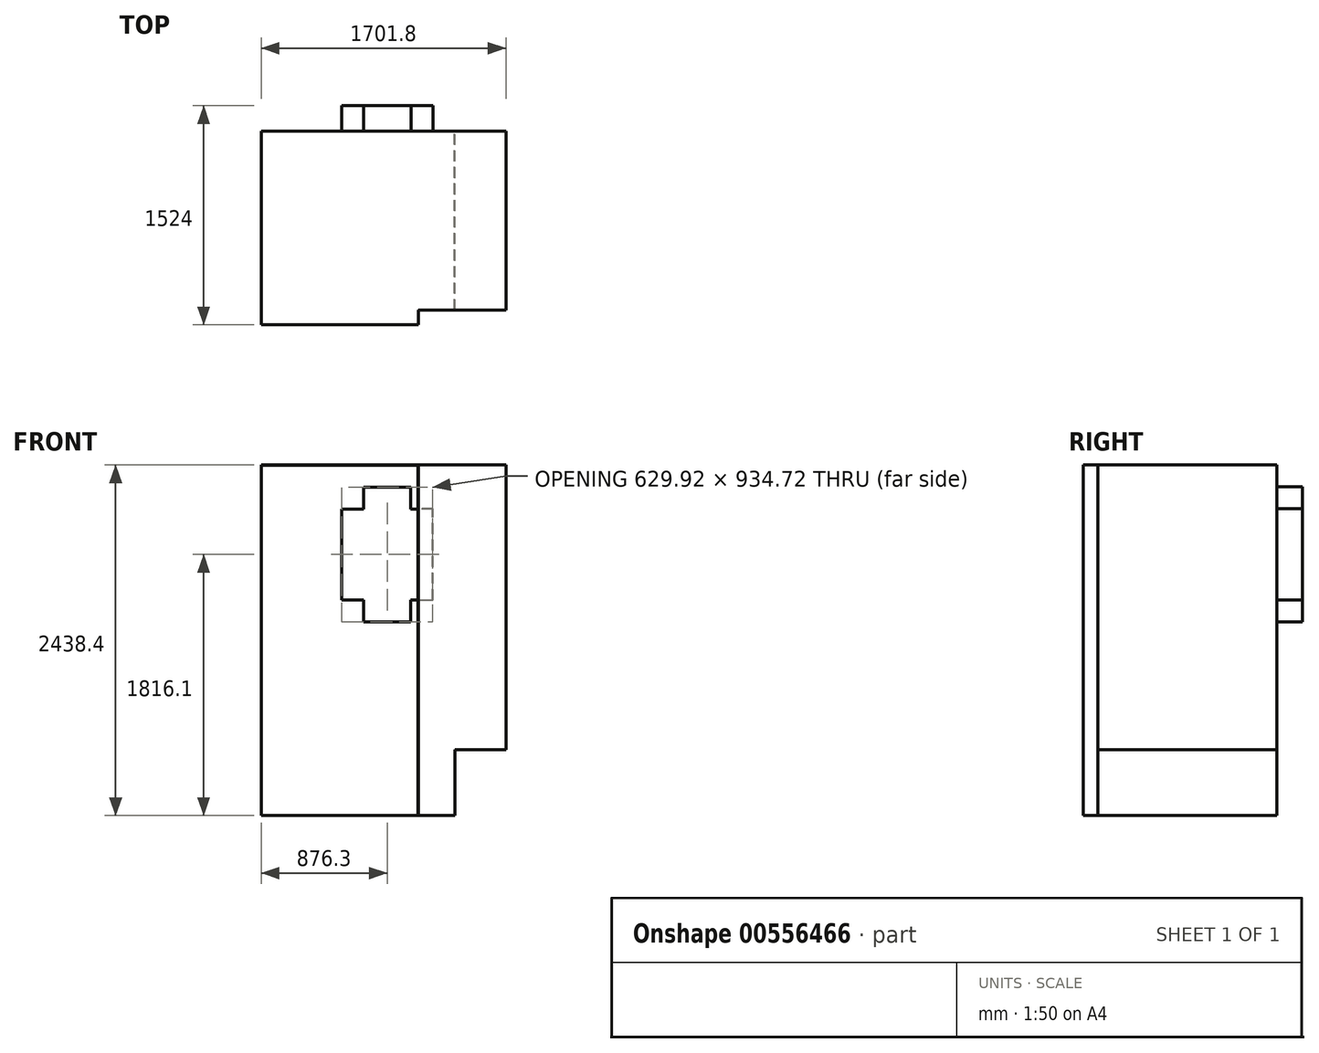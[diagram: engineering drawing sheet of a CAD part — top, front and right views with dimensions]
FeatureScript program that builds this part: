
annotation { "Feature Type Name" : "Feature", "Feature Type Description" : "" }
export const myFeature = defineFeature(function(context is Context, id is Id, definition is map)
    precondition{}
    {
        {
            var Q0;
            Q0=qCreatedBy(makeId("Front.planeOp"),FACE);
            var sketch = newSketch(context, id + "F0", { "sketchPlane" : qUnion([Q0])});
            skLineSegment(sketch, "E0", {"start": v(0, 0) * mm, "end": v(1346.2, 0) * mm});
            skLineSegment(sketch, "E1", {"start": v(1346.2, 0) * mm, "end": v(1346.2, 457.2) * mm});
            skLineSegment(sketch, "E2", {"start": v(1346.2, 457.2) * mm, "end": v(1701.8, 457.2) * mm});
            skLineSegment(sketch, "E3", {"start": v(1701.8, 457.2) * mm, "end": v(1701.8, 2438.4) * mm});
            skLineSegment(sketch, "E4", {"start": v(1701.8, 2438.4) * mm, "end": v(0, 2438.4) * mm});
            skLineSegment(sketch, "E5", {"start": v(0, 2438.4) * mm, "end": v(0, 0) * mm});
            skSolve(sketch);
        }
        {
            var Q0;
            Q0 = qSketchRegion(id + "F0", true);
            extrude(context, id + "F1", {"entities" : qUnion([Q0]), "depth" : 1244.6 * mm, "offsetDistance" : 25.4 * mm});
        }
        {
            var Q0;
            Q0=qCreatedBy(makeId("Front.planeOp"),FACE);
            var sketch = newSketch(context, id + "F2", { "sketchPlane" : qUnion([Q0])});
            skLineSegment(sketch, "E6", {"start": v(711.2, 1346.2) * mm, "end": v(1041.4, 1346.2) * mm});
            skLineSegment(sketch, "E7", {"start": v(1041.4, 1346.2) * mm, "end": v(1041.4, 1498.6) * mm});
            skLineSegment(sketch, "E8", {"start": v(1041.4, 1498.6) * mm, "end": v(1193.8, 1498.6) * mm});
            skLineSegment(sketch, "E9", {"start": v(1193.8, 1498.6) * mm, "end": v(1193.8, 2133.6) * mm});
            skLineSegment(sketch, "E10", {"start": v(1193.8, 2133.6) * mm, "end": v(1041.4, 2133.6) * mm});
            skLineSegment(sketch, "E11", {"start": v(1041.4, 2133.6) * mm, "end": v(1041.4, 2286) * mm});
            skLineSegment(sketch, "E12", {"start": v(1041.4, 2286) * mm, "end": v(711.2, 2286) * mm});
            skLineSegment(sketch, "E13", {"start": v(711.2, 2286) * mm, "end": v(711.2, 2133.6) * mm});
            skLineSegment(sketch, "E14", {"start": v(711.2, 2133.6) * mm, "end": v(558.8, 2133.6) * mm});
            skLineSegment(sketch, "E15", {"start": v(558.8, 2133.6) * mm, "end": v(558.8, 1498.6) * mm});
            skLineSegment(sketch, "E16", {"start": v(558.8, 1498.6) * mm, "end": v(711.2, 1498.6) * mm});
            skLineSegment(sketch, "E17", {"start": v(711.2, 1498.6) * mm, "end": v(711.2, 1346.2) * mm});
            skSolve(sketch);
        }
        {
            var Q0;
            Q0 = qSketchRegion(id + "F2", true);
            extrude(context, id + "F3", {"entities" : qUnion([Q0]), "operationType" : NewBodyOperationType.ADD, "oppositeDirection" : true, "depth" : 177.8 * mm, "offsetDistance" : 25.4 * mm});
        }
        {
            var Q0;
            Q0=makeQuery(id+"F1.opExtrude","CAP_FACE",FACE,{"disambiguationData":[OSD([sQuery(id+"F0.wireOp",EDGE,"E0"),sQuery(id+"F0.wireOp",EDGE,"E1"),sQuery(id+"F0.wireOp",EDGE,"E2"),sQuery(id+"F0.wireOp",EDGE,"E3"),sQuery(id+"F0.wireOp",EDGE,"E4"),sQuery(id+"F0.wireOp",EDGE,"E5")])],"isStart":false});
            var sketch = newSketch(context, id + "F4", { "sketchPlane" : qUnion([Q0])});
            skLineSegment(sketch, "E18", {"start": v(0, 2438.4) * mm, "end": v(0, 0) * mm});
            skLineSegment(sketch, "E19", {"start": v(0, 0) * mm, "end": v(1092.2, 0) * mm});
            skLineSegment(sketch, "E20", {"start": v(1092.2, 0) * mm, "end": v(1092.2, 2438.4) * mm});
            skLineSegment(sketch, "E21", {"start": v(1092.2, 2438.4) * mm, "end": v(0, 2438.4) * mm});
            skSolve(sketch);
        }
        {
            var Q0;
            Q0 = qSketchRegion(id + "F4", true);
            extrude(context, id + "F5", {"entities" : qUnion([Q0]), "operationType" : NewBodyOperationType.ADD, "depth" : 101.6 * mm, "offsetDistance" : 25.4 * mm});
        }
        {
            var Q0;
            Q0=makeQuery(id+"F5.opExtrude","CAP_FACE",FACE,{"disambiguationData":[OSD([sQuery(id+"F4.wireOp",EDGE,"E18"),sQuery(id+"F4.wireOp",EDGE,"E19"),sQuery(id+"F4.wireOp",EDGE,"E20"),sQuery(id+"F4.wireOp",EDGE,"E21")])],"isStart":false});
            var Q1;
            Q1=makeQuery(id+"F3.opExtrude","CAP_FACE",FACE,{"disambiguationData":[OSD([sQuery(id+"F2.wireOp",EDGE,"E6"),sQuery(id+"F2.wireOp",EDGE,"E7"),sQuery(id+"F2.wireOp",EDGE,"E8"),sQuery(id+"F2.wireOp",EDGE,"E9"),sQuery(id+"F2.wireOp",EDGE,"E10"),sQuery(id+"F2.wireOp",EDGE,"E11"),sQuery(id+"F2.wireOp",EDGE,"E12"),sQuery(id+"F2.wireOp",EDGE,"E13"),sQuery(id+"F2.wireOp",EDGE,"E14"),sQuery(id+"F2.wireOp",EDGE,"E15"),sQuery(id+"F2.wireOp",EDGE,"E16"),sQuery(id+"F2.wireOp",EDGE,"E17")])],"isStart":false});
            shell(context, id + "F6", {"entities" : qUnion([Q0, Q1]), "thickness" : 2.54 * mm});
        }
    });
